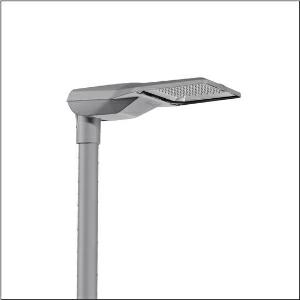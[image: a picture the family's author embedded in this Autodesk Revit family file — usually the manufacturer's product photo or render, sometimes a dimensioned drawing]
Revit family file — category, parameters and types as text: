
# Revit family: streetlight_sl_21_iq_midi___st0_8a_5xe3c41d08mb_0a8a
name_source: partatom
category: Lighting Fixtures
units: mm (PartAtom-declared; Revit-internal decimal feet)

## family parameters
Cut with Voids When Loaded = No
Host = Face
Light Source = No
Part Type = Normal
Room Calculation Point = No
Round Connector Dimension = Use Diameter
Shared = No

## types (1)
- --- (1 x LED, 20360 lm, 146.7 W, 4000K)
    Apparent Load = 147 VA
    CIE Flux Codes = 38 75 97 100 100
    Color Rendering = 70
    Color Temperature = 4000K
    Default Elevation = 1800 mm
    Description = Streetlight SL 21 iQ midi, mast luminaire, primary light control with lens, of PMMA, primary optical cover: cover, of toughened safety glass, transparent, light distribution: ST0.8a, light emission: direct distribution, primary light characteristic: asymmetric, installation type: post-top, side-entry, LED, High Power LED, rated luminous flux: 20.360lm, luminous efficacy: 139lm/W, light colour: 740, colour temperature: 4000K, control: Auto-Match, Temp-Guard, Lumen-Switch, Night-Set, Smart-Wire, Light-Fading, Desk-Remote (wireless, voltage-free reading and setting of iQ features in the workshop via application-optimized NFC function/RFID function), optimised constant luminous flux control (CLO 2.0), presetting dimming linear, mains connection: 230..240V, AC, 50/60Hz, start of lifetime: 147W, end of service life: 161W, reduction: 62W, luminaire housing, of diecast aluminium, powder-coated, Siteco® metallic grey (DB 702S), corrosivity category C5 mid according to DIN EN ISO 12944, please order mast flange separately, inclination adjustable: 0°, 5°, 10°, 15°, sealing non-destructively replaceable, multi-level sealing system, length: 644mm, width: 335mm, height: 110mm, mast flange for spigot size: 42mm (side-entry): 5XC10008XM4, 60/48mm (side-entry/post-top): 5XC10108XM2, 76/60mm (side-entry/post-top): 5XC10108XM1, protection rating (complete): IP66, insulation class (complete): insulation class II (safety insulation), certification: CE, ENEC, ENEC+, VDE, impact resistance: IK09, permissible operating ambient temperature for outdoor applications: -40..+50°C, standard-compliant lighting for roads and squares, packaging unit: 1 piece

Light Distribution: ST0.8a
    Height = 111 mm
    Lamp = 1 x LED
    Lamp Light Flux = 20360 lm
    Lamp Power = 146.7 W
    Lamp count = 1
    Length = 644 mm
    Luminous efficacy = 139 lm/W
    Manufacturer = Siteco
    ModVariant = No
    Model = 5XE3C41D08MB
    Number of Poles = 1
    OnlyDefault = Yes
    Power Factor = 1
    Product Name = Streetlight SL 21 iQ midi | ST0.8a
    Product group = mast luminaire | pylon top
    ProductGroupID = 6100
    Protection Class = Protection class II
    Protection Degree = IP 66
    RLX_Detail_Level = 1
    RLX_Emergency_Light_Flux = 0 lm
    RLX_Emergency_Type = 0
    RLX_Emergency_Type_DB = No
    RlxData = <blob elided: 91161 chars, md5=4a0d17ea>
    Socket = socket
    Standby Power = 0 W
    System Light Flux = 20360 lm
    System Power = 147 W
    Type Comments = factory setting: luminous flux: 100 % | dim-lin: 254 | 753 mA
    Type Image = l_1004298.jpg
    URL = http://relux.com
    VarID = @adj_138011
    Voltage = 0 V
    Weight = 0.00 kg
    Width = 336 mm

## geometry (parser evidence)
native form markers: Blend x4, Sweep x11
no freeform markers — native parametric forms only
